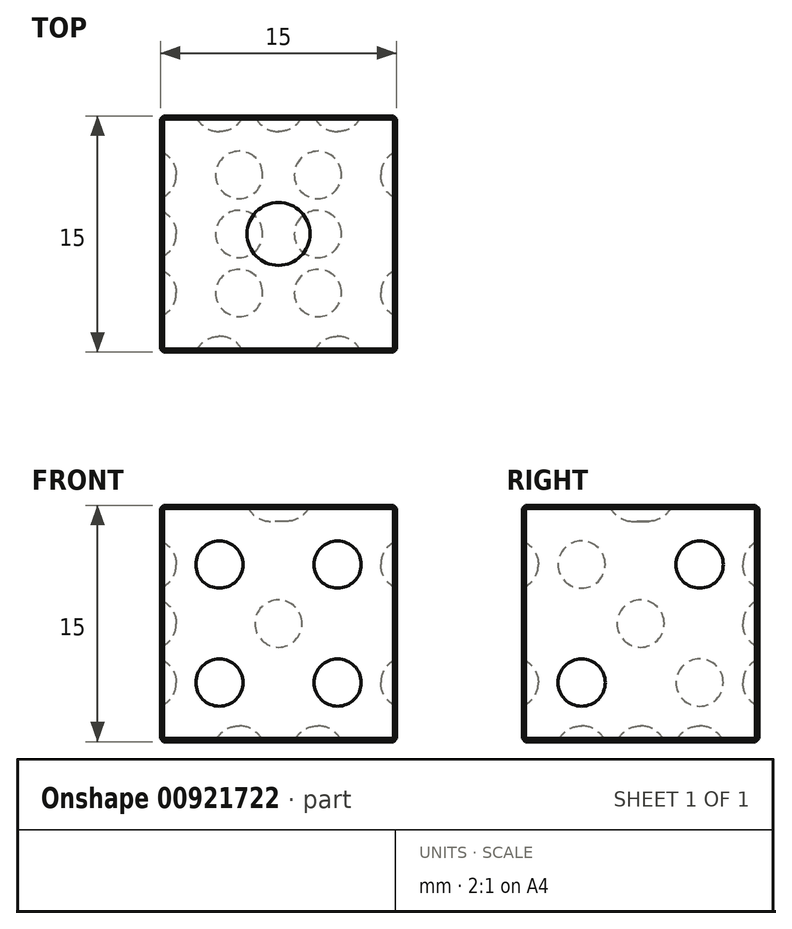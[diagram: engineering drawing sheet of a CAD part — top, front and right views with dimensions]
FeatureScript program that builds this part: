
annotation { "Feature Type Name" : "Feature", "Feature Type Description" : "" }
export const myFeature = defineFeature(function(context is Context, id is Id, definition is map)
    precondition{}
    {
        {
            var Q0;
            Q0=qCreatedBy(makeId("Top.planeOp"),FACE);
            var sketch = newSketch(context, id + "F0", { "sketchPlane" : qUnion([Q0])});
            skLineSegment(sketch, "E0.bottom", {"start": v(0, 0) * mm, "end": v(15, 0) * mm});
            skLineSegment(sketch, "E0.top", {"start": v(0, 15) * mm, "end": v(15, 15) * mm});
            skLineSegment(sketch, "E0.left", {"start": v(0, 0) * mm, "end": v(0, 15) * mm});
            skLineSegment(sketch, "E0.right", {"start": v(15, 0) * mm, "end": v(15, 15) * mm});
            skSolve(sketch);
        }
        {
            var Q0;
            Q0=makeQuery(id+"F0.imprint","IMPRINT",FACE,{"disambiguationData":[TD([[makeQuery(id+"F0.imprint","IMPRINT",EDGE,{"derivedFrom":sQuery(id+"F0.wireOp",EDGE,"E0.bottom")}),1.0]])]});
            extrude(context, id + "F1", {"entities" : qUnion([Q0]), "depth" : 15 * mm, "offsetDistance" : 25 * mm});
        }
        {
            var Q0;
            Q0=makeQuery(id+"F1.opExtrude","CAP_FACE",FACE,{"disambiguationData":[OSD([sQuery(id+"F0.wireOp",EDGE,"E0.bottom"),sQuery(id+"F0.wireOp",EDGE,"E0.top"),sQuery(id+"F0.wireOp",EDGE,"E0.left"),sQuery(id+"F0.wireOp",EDGE,"E0.right")])],"isStart":false});
            var sketch = newSketch(context, id + "F2", { "sketchPlane" : qUnion([Q0])});
            skCircle(sketch, "E1", {"center": v(7.5, 7.5) * mm, "radius": 2 * mm});
            skPoint(sketch, "E1.centerSnap0", {"position": v(0, 7.5) * mm});
            skPoint(sketch, "E1.centerSnap1", {"position": v(7.5, 15) * mm});
            skSolve(sketch);
        }
        {
            var Q0;
            Q0=makeQuery(id+"F2.imprint","IMPRINT",FACE,{"disambiguationData":[TD([[makeQuery(id+"F2.imprint","IMPRINT",EDGE,{"derivedFrom":sQuery(id+"F2.wireOp",EDGE,"E1")}),1.0]])]});
            extrude(context, id + "F3", {"entities" : qUnion([Q0]), "operationType" : NewBodyOperationType.REMOVE, "oppositeDirection" : true, "depth" : 1 * mm, "offsetDistance" : 25 * mm});
        }
        {
            var Q0;
            Q0=makeQuery(id+"F1.opExtrude","CAP_FACE",FACE,{"disambiguationData":[OSD([sQuery(id+"F0.wireOp",EDGE,"E0.bottom"),sQuery(id+"F0.wireOp",EDGE,"E0.top"),sQuery(id+"F0.wireOp",EDGE,"E0.left"),sQuery(id+"F0.wireOp",EDGE,"E0.right")])],"isStart":true});
            var sketch = newSketch(context, id + "F4", { "sketchPlane" : qUnion([Q0])});
            skLineSegment(sketch, "E2", {"start": v(5, 0) * mm, "end": v(5, -15) * mm, "construction": true});
            skLineSegment(sketch, "E3", {"start": v(10, 0) * mm, "end": v(10, -15) * mm, "construction": true});
            skLineSegment(sketch, "E4", {"start": v(0, -3.75) * mm, "end": v(15, -3.75) * mm, "construction": true});
            skLineSegment(sketch, "E5", {"start": v(0, -7.5) * mm, "end": v(15, -7.5) * mm, "construction": true});
            skLineSegment(sketch, "E6", {"start": v(0, -11.25) * mm, "end": v(15, -11.25) * mm, "construction": true});
            skCircle(sketch, "E7", {"center": v(5, -3.75) * mm, "radius": 1.5 * mm});
            skCircle(sketch, "E8", {"center": v(10, -3.75) * mm, "radius": 1.5 * mm});
            skCircle(sketch, "E9", {"center": v(10, -7.5) * mm, "radius": 1.5 * mm});
            skCircle(sketch, "E10", {"center": v(5, -7.5) * mm, "radius": 1.5 * mm});
            skCircle(sketch, "E11", {"center": v(5, -11.25) * mm, "radius": 1.5 * mm});
            skCircle(sketch, "E12", {"center": v(10, -11.25) * mm, "radius": 1.5 * mm});
            skSolve(sketch);
        }
        {
            var Q0;
            Q0 = qSketchRegion(id + "F4", true);
            extrude(context, id + "F5", {"entities" : qUnion([Q0]), "operationType" : NewBodyOperationType.REMOVE, "oppositeDirection" : true, "depth" : 1 * mm, "offsetDistance" : 25 * mm});
        }
        {
            var Q0;
            Q0=makeQuery(id+"F1.opExtrude","SWEPT_FACE",FACE,{"disambiguationData":[OSD([sQuery(id+"F0.wireOp",EDGE,"E0.right")])]});
            var sketch = newSketch(context, id + "F6", { "sketchPlane" : qUnion([Q0])});
            skLineSegment(sketch, "E13", {"start": v(15, 15) * mm, "end": v(0, 0) * mm, "construction": true});
            skLineSegment(sketch, "E14", {"start": v(3.75, 15) * mm, "end": v(3.75, 0) * mm, "construction": true});
            skLineSegment(sketch, "E15", {"start": v(11.25, 15) * mm, "end": v(11.25, 0) * mm, "construction": true});
            skCircle(sketch, "E16", {"center": v(3.75, 3.75) * mm, "radius": 1.5 * mm});
            skCircle(sketch, "E17", {"center": v(11.25, 11.25) * mm, "radius": 1.5 * mm});
            skSolve(sketch);
        }
        {
            var Q0;
            Q0 = qSketchRegion(id + "F6", true);
            extrude(context, id + "F7", {"entities" : qUnion([Q0]), "operationType" : NewBodyOperationType.REMOVE, "oppositeDirection" : true, "depth" : 1 * mm, "offsetDistance" : 25 * mm});
        }
        {
            var Q0;
            Q0=makeQuery(id+"F1.opExtrude","SWEPT_FACE",FACE,{"disambiguationData":[OSD([sQuery(id+"F0.wireOp",EDGE,"E0.left")])]});
            var sketch = newSketch(context, id + "F8", { "sketchPlane" : qUnion([Q0])});
            skLineSegment(sketch, "E18", {"start": v(0, 15) * mm, "end": v(-15, 0) * mm, "construction": true});
            skLineSegment(sketch, "E19", {"start": v(-15, 15) * mm, "end": v(0, 0) * mm, "construction": true});
            skLineSegment(sketch, "E20", {"start": v(-11.25, 15) * mm, "end": v(-11.25, 0) * mm, "construction": true});
            skLineSegment(sketch, "E21", {"start": v(-3.75, 15) * mm, "end": v(-3.75, 0) * mm, "construction": true});
            skCircle(sketch, "E22", {"center": v(-11.25, 11.25) * mm, "radius": 1.5 * mm});
            skCircle(sketch, "E23", {"center": v(-7.5, 7.5) * mm, "radius": 1.5 * mm});
            skCircle(sketch, "E24", {"center": v(-11.25, 3.75) * mm, "radius": 1.5 * mm});
            skCircle(sketch, "E25", {"center": v(-3.75, 3.75) * mm, "radius": 1.5 * mm});
            skCircle(sketch, "E26", {"center": v(-3.75, 11.25) * mm, "radius": 1.5 * mm});
            skSolve(sketch);
        }
        {
            var Q0;
            Q0 = qSketchRegion(id + "F8", true);
            extrude(context, id + "F9", {"entities" : qUnion([Q0]), "operationType" : NewBodyOperationType.REMOVE, "oppositeDirection" : true, "depth" : 1 * mm, "offsetDistance" : 25 * mm});
        }
        {
            var Q0;
            Q0=makeQuery(id+"F1.opExtrude","SWEPT_FACE",FACE,{"disambiguationData":[OSD([sQuery(id+"F0.wireOp",EDGE,"E0.top")])]});
            var sketch = newSketch(context, id + "F10", { "sketchPlane" : qUnion([Q0])});
            skLineSegment(sketch, "E27", {"start": v(0, 15) * mm, "end": v(-15, 0) * mm, "construction": true});
            skLineSegment(sketch, "E28", {"start": v(-7.5, 15) * mm, "end": v(-7.5, 0) * mm, "construction": true});
            skLineSegment(sketch, "E29", {"start": v(-11.25, 15) * mm, "end": v(-11.25, 0) * mm, "construction": true});
            skLineSegment(sketch, "E30", {"start": v(-3.75, 15) * mm, "end": v(-3.75, 0) * mm, "construction": true});
            skCircle(sketch, "E31", {"center": v(-3.75, 11.25) * mm, "radius": 1.5 * mm});
            skCircle(sketch, "E32", {"center": v(-7.5, 7.5) * mm, "radius": 1.5 * mm});
            skCircle(sketch, "E33", {"center": v(-11.25, 3.75) * mm, "radius": 1.5 * mm});
            skSolve(sketch);
        }
        {
            var Q0;
            Q0 = qSketchRegion(id + "F10", true);
            extrude(context, id + "F11", {"entities" : qUnion([Q0]), "operationType" : NewBodyOperationType.REMOVE, "oppositeDirection" : true, "depth" : 1 * mm, "offsetDistance" : 25 * mm});
        }
        {
            var Q0;
            Q0=makeQuery(id+"F1.opExtrude","SWEPT_FACE",FACE,{"disambiguationData":[OSD([sQuery(id+"F0.wireOp",EDGE,"E0.bottom")])]});
            var sketch = newSketch(context, id + "F12", { "sketchPlane" : qUnion([Q0])});
            skLineSegment(sketch, "E34.bottom", {"start": v(11.25, 11.25) * mm, "end": v(3.75, 11.25) * mm, "construction": true});
            skLineSegment(sketch, "E34.top", {"start": v(11.25, 3.75) * mm, "end": v(3.75, 3.75) * mm, "construction": true});
            skLineSegment(sketch, "E34.left", {"start": v(11.25, 11.25) * mm, "end": v(11.25, 3.75) * mm, "construction": true});
            skLineSegment(sketch, "E34.right", {"start": v(3.75, 11.25) * mm, "end": v(3.75, 3.75) * mm, "construction": true});
            skPoint(sketch, "E34.middle", {"position": v(7.5, 7.5) * mm});
            skPoint(sketch, "E34.middle.positionSnap0", {"position": v(7.5, 15) * mm});
            skPoint(sketch, "E34.middle.positionSnap1", {"position": v(0, 7.5) * mm});
            skPoint(sketch, "E34.centerSnap0", {"position": v(7.5, 15) * mm});
            skPoint(sketch, "E34.centerSnap1", {"position": v(0, 7.5) * mm});
            skCircle(sketch, "E35", {"center": v(3.75, 11.25) * mm, "radius": 1.5 * mm});
            skCircle(sketch, "E36", {"center": v(11.25, 11.25) * mm, "radius": 1.5 * mm});
            skCircle(sketch, "E37", {"center": v(11.25, 3.75) * mm, "radius": 1.5 * mm});
            skCircle(sketch, "E38", {"center": v(3.75, 3.75) * mm, "radius": 1.5 * mm});
            skSolve(sketch);
        }
        {
            var Q0;
            Q0 = qSketchRegion(id + "F12", true);
            extrude(context, id + "F13", {"entities" : qUnion([Q0]), "operationType" : NewBodyOperationType.REMOVE, "oppositeDirection" : true, "depth" : 1 * mm, "offsetDistance" : 25 * mm});
        }
        {
            var Q0;
            Q0=makeQuery(id+"F9.boolean.opBoolean","COPY",EDGE,{"derivedFrom":makeQuery(id+"F9.opExtrude","CAP_EDGE",EDGE,{"disambiguationData":[OSD([sQuery(id+"F8.wireOp",EDGE,"E24")])],"isStart":false})});
            var Q1;
            Q1=makeQuery(id+"F9.boolean.opBoolean","COPY",EDGE,{"derivedFrom":makeQuery(id+"F9.opExtrude","CAP_EDGE",EDGE,{"disambiguationData":[OSD([sQuery(id+"F8.wireOp",EDGE,"E23")])],"isStart":false})});
            var Q2;
            Q2=makeQuery(id+"F9.boolean.opBoolean","COPY",EDGE,{"derivedFrom":makeQuery(id+"F9.opExtrude","CAP_EDGE",EDGE,{"disambiguationData":[OSD([sQuery(id+"F8.wireOp",EDGE,"E22")])],"isStart":false})});
            var Q3;
            Q3=makeQuery(id+"F9.boolean.opBoolean","COPY",EDGE,{"derivedFrom":makeQuery(id+"F9.opExtrude","CAP_EDGE",EDGE,{"disambiguationData":[OSD([sQuery(id+"F8.wireOp",EDGE,"E25")])],"isStart":false})});
            var Q4;
            Q4=makeQuery(id+"F9.boolean.opBoolean","COPY",EDGE,{"derivedFrom":makeQuery(id+"F9.opExtrude","CAP_EDGE",EDGE,{"disambiguationData":[OSD([sQuery(id+"F8.wireOp",EDGE,"E26")])],"isStart":false})});
            var Q5;
            Q5=makeQuery(id+"F11.boolean.opBoolean","COPY",EDGE,{"derivedFrom":makeQuery(id+"F11.opExtrude","CAP_EDGE",EDGE,{"disambiguationData":[OSD([sQuery(id+"F10.wireOp",EDGE,"E31")])],"isStart":false})});
            var Q6;
            Q6=makeQuery(id+"F11.boolean.opBoolean","COPY",EDGE,{"derivedFrom":makeQuery(id+"F11.opExtrude","CAP_EDGE",EDGE,{"disambiguationData":[OSD([sQuery(id+"F10.wireOp",EDGE,"E32")])],"isStart":false})});
            var Q7;
            Q7=makeQuery(id+"F11.boolean.opBoolean","COPY",EDGE,{"derivedFrom":makeQuery(id+"F11.opExtrude","CAP_EDGE",EDGE,{"disambiguationData":[OSD([sQuery(id+"F10.wireOp",EDGE,"E33")])],"isStart":false})});
            var Q8;
            Q8=makeQuery(id+"F5.boolean.opBoolean","COPY",EDGE,{"derivedFrom":makeQuery(id+"F5.opExtrude","CAP_EDGE",EDGE,{"disambiguationData":[OSD([sQuery(id+"F4.wireOp",EDGE,"E12")])],"isStart":false})});
            var Q9;
            Q9=makeQuery(id+"F5.boolean.opBoolean","COPY",EDGE,{"derivedFrom":makeQuery(id+"F5.opExtrude","CAP_EDGE",EDGE,{"disambiguationData":[OSD([sQuery(id+"F4.wireOp",EDGE,"E9")])],"isStart":false})});
            var Q10;
            Q10=makeQuery(id+"F5.boolean.opBoolean","COPY",EDGE,{"derivedFrom":makeQuery(id+"F5.opExtrude","CAP_EDGE",EDGE,{"disambiguationData":[OSD([sQuery(id+"F4.wireOp",EDGE,"E11")])],"isStart":false})});
            var Q11;
            Q11=makeQuery(id+"F5.boolean.opBoolean","COPY",EDGE,{"derivedFrom":makeQuery(id+"F5.opExtrude","CAP_EDGE",EDGE,{"disambiguationData":[OSD([sQuery(id+"F4.wireOp",EDGE,"E10")])],"isStart":false})});
            var Q12;
            Q12=makeQuery(id+"F5.boolean.opBoolean","COPY",EDGE,{"derivedFrom":makeQuery(id+"F5.opExtrude","CAP_EDGE",EDGE,{"disambiguationData":[OSD([sQuery(id+"F4.wireOp",EDGE,"E7")])],"isStart":false})});
            var Q13;
            Q13=makeQuery(id+"F5.boolean.opBoolean","COPY",EDGE,{"derivedFrom":makeQuery(id+"F5.opExtrude","CAP_EDGE",EDGE,{"disambiguationData":[OSD([sQuery(id+"F4.wireOp",EDGE,"E8")])],"isStart":false})});
            var Q14;
            Q14=makeQuery(id+"F7.boolean.opBoolean","COPY",EDGE,{"derivedFrom":makeQuery(id+"F7.opExtrude","CAP_EDGE",EDGE,{"disambiguationData":[OSD([sQuery(id+"F6.wireOp",EDGE,"E16")])],"isStart":false})});
            var Q15;
            Q15=makeQuery(id+"F7.boolean.opBoolean","COPY",EDGE,{"derivedFrom":makeQuery(id+"F7.opExtrude","CAP_EDGE",EDGE,{"disambiguationData":[OSD([sQuery(id+"F6.wireOp",EDGE,"E17")])],"isStart":false})});
            var Q16;
            Q16=makeQuery(id+"F3.boolean.opBoolean","COPY",EDGE,{"derivedFrom":makeQuery(id+"F3.opExtrude","CAP_EDGE",EDGE,{"disambiguationData":[OSD([sQuery(id+"F2.wireOp",EDGE,"E1")])],"isStart":false})});
            var Q17;
            Q17=makeQuery(id+"F13.boolean.opBoolean","COPY",EDGE,{"derivedFrom":makeQuery(id+"F13.opExtrude","CAP_EDGE",EDGE,{"disambiguationData":[OSD([sQuery(id+"F12.wireOp",EDGE,"E35")])],"isStart":false})});
            var Q18;
            Q18=makeQuery(id+"F13.boolean.opBoolean","COPY",EDGE,{"derivedFrom":makeQuery(id+"F13.opExtrude","CAP_EDGE",EDGE,{"disambiguationData":[OSD([sQuery(id+"F12.wireOp",EDGE,"E36")])],"isStart":false})});
            var Q19;
            Q19=makeQuery(id+"F13.boolean.opBoolean","COPY",EDGE,{"derivedFrom":makeQuery(id+"F13.opExtrude","CAP_EDGE",EDGE,{"disambiguationData":[OSD([sQuery(id+"F12.wireOp",EDGE,"E37")])],"isStart":false})});
            var Q20;
            Q20=makeQuery(id+"F13.boolean.opBoolean","COPY",EDGE,{"derivedFrom":makeQuery(id+"F13.opExtrude","CAP_EDGE",EDGE,{"disambiguationData":[OSD([sQuery(id+"F12.wireOp",EDGE,"E38")])],"isStart":false})});
            fillet(context, id + "F14", {"entities" : qUnion([Q0, Q1, Q2, Q3, Q4, Q5, Q6, Q7, Q8, Q9, Q10, Q11, Q12, Q13, Q14, Q15, Q16, Q17, Q18, Q19, Q20]), "radius" : 1.6 * mm, "tangentPropagation" : true, "allowEdgeOverflow" : false});
        }
        {
            var Q0;
            Q0=makeQuery(id+"F1.opExtrude","SWEPT_EDGE",EDGE,{"disambiguationData":[OSD([sQuery(id+"F0.wireOp",EDGE,"E0.bottom"),sQuery(id+"F0.wireOp",EDGE,"E0.right")])]});
            var Q1;
            Q1=makeQuery(id+"F1.opExtrude","CAP_EDGE",EDGE,{"disambiguationData":[OSD([sQuery(id+"F0.wireOp",EDGE,"E0.bottom")])],"isStart":true});
            var Q2;
            Q2=makeQuery(id+"F1.opExtrude","CAP_EDGE",EDGE,{"disambiguationData":[OSD([sQuery(id+"F0.wireOp",EDGE,"E0.right")])],"isStart":true});
            var Q3;
            Q3=makeQuery(id+"F1.opExtrude","CAP_EDGE",EDGE,{"disambiguationData":[OSD([sQuery(id+"F0.wireOp",EDGE,"E0.left")])],"isStart":true});
            var Q4;
            Q4=makeQuery(id+"F1.opExtrude","SWEPT_EDGE",EDGE,{"disambiguationData":[OSD([sQuery(id+"F0.wireOp",EDGE,"E0.bottom"),sQuery(id+"F0.wireOp",EDGE,"E0.left")])]});
            var Q5;
            Q5=makeQuery(id+"F1.opExtrude","SWEPT_EDGE",EDGE,{"disambiguationData":[OSD([sQuery(id+"F0.wireOp",EDGE,"E0.top"),sQuery(id+"F0.wireOp",EDGE,"E0.left")])]});
            var Q6;
            Q6=makeQuery(id+"F1.opExtrude","CAP_EDGE",EDGE,{"disambiguationData":[OSD([sQuery(id+"F0.wireOp",EDGE,"E0.top")])],"isStart":true});
            var Q7;
            Q7=makeQuery(id+"F1.opExtrude","CAP_EDGE",EDGE,{"disambiguationData":[OSD([sQuery(id+"F0.wireOp",EDGE,"E0.top")])],"isStart":false});
            var Q8;
            Q8=makeQuery(id+"F1.opExtrude","CAP_EDGE",EDGE,{"disambiguationData":[OSD([sQuery(id+"F0.wireOp",EDGE,"E0.left")])],"isStart":false});
            var Q9;
            Q9=makeQuery(id+"F1.opExtrude","CAP_EDGE",EDGE,{"disambiguationData":[OSD([sQuery(id+"F0.wireOp",EDGE,"E0.bottom")])],"isStart":false});
            var Q10;
            Q10=makeQuery(id+"F1.opExtrude","CAP_EDGE",EDGE,{"disambiguationData":[OSD([sQuery(id+"F0.wireOp",EDGE,"E0.right")])],"isStart":false});
            var Q11;
            Q11=makeQuery(id+"F1.opExtrude","SWEPT_EDGE",EDGE,{"disambiguationData":[OSD([sQuery(id+"F0.wireOp",EDGE,"E0.top"),sQuery(id+"F0.wireOp",EDGE,"E0.right")])]});
            chamfer(context, id + "F15", {"entities" : qUnion([Q0, Q1, Q2, Q3, Q4, Q5, Q6, Q7, Q8, Q9, Q10, Q11]), "width" : 0.2 * mm, "tangentPropagation" : true});
        }
    });
